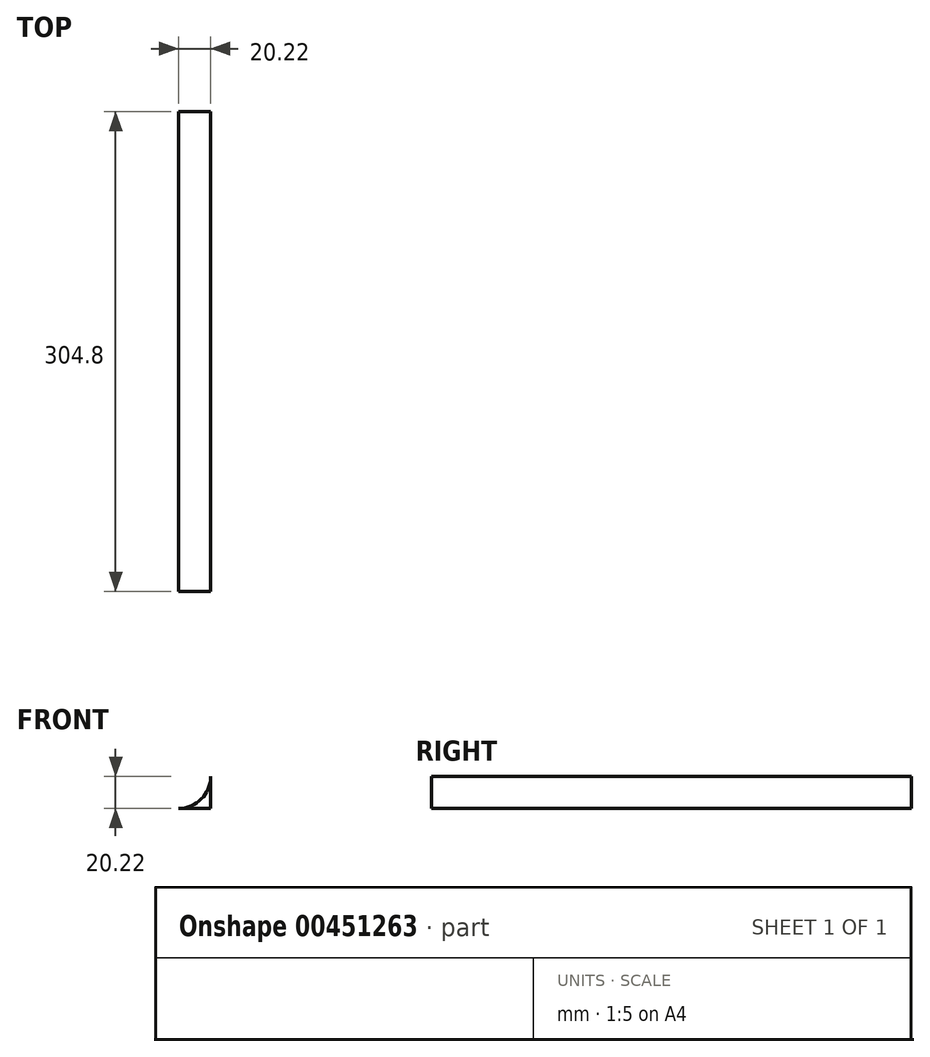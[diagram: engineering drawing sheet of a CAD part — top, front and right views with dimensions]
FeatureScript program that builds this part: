
annotation { "Feature Type Name" : "Feature", "Feature Type Description" : "" }
export const myFeature = defineFeature(function(context is Context, id is Id, definition is map)
    precondition{}
    {
        {
            var Q0;
            Q0=qCreatedBy(makeId("Front.planeOp"),FACE);
            var sketch = newSketch(context, id + "F0", { "sketchPlane" : qUnion([Q0])});
            skLineSegment(sketch, "E0", {"start": v(20.22, 0) * mm, "end": v(20.22, -20.22) * mm});
            skLineSegment(sketch, "E1", {"start": v(20.22, -20.22) * mm, "end": v(0, -20.22) * mm});
            skArc(sketch, "E2", {"start": v(0, -20.22) * mm, "mid": v(14.3, -14.3) * mm, "end": v(20.22, 0) * mm});
            skSolve(sketch);
        }
        {
            var Q0;
            Q0=makeQuery(id+"F0.imprint","IMPRINT",FACE,{"disambiguationData":[TD([[makeQuery(id+"F0.imprint","IMPRINT",EDGE,{"derivedFrom":sQuery(id+"F0.wireOp",EDGE,"E0")}),-1.0]])]});
            extrude(context, id + "F1", {"entities" : qUnion([Q0]), "depth" : 304.8 * mm});
        }
    });
